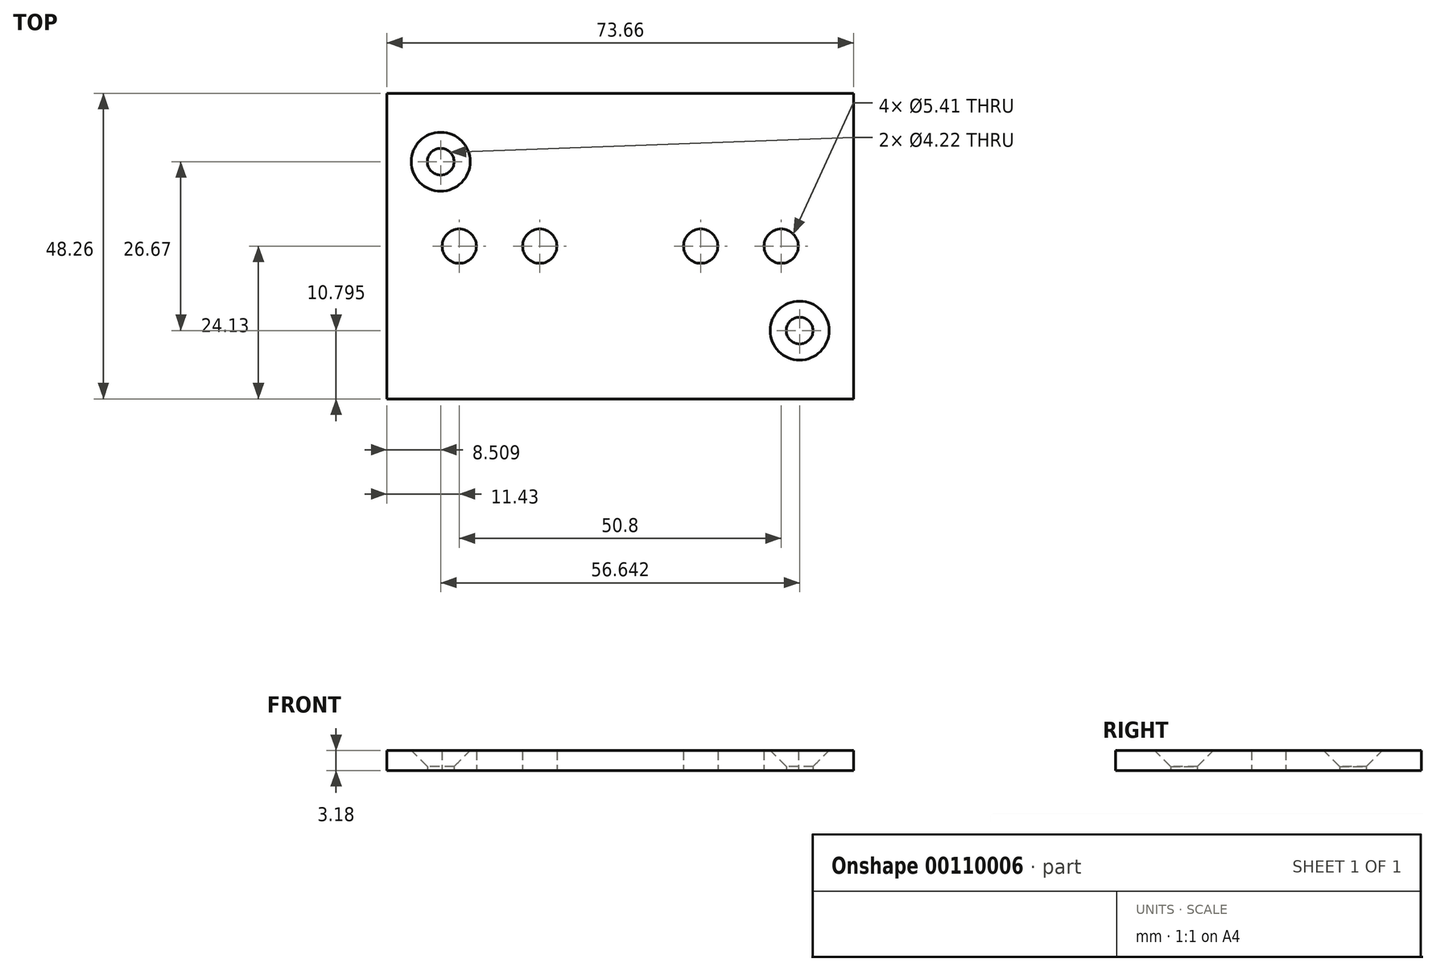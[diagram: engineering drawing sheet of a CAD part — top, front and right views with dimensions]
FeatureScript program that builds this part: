
annotation { "Feature Type Name" : "Feature", "Feature Type Description" : "" }
export const myFeature = defineFeature(function(context is Context, id is Id, definition is map)
    precondition{}
    {
        {
            var Q0;
            Q0=qCreatedBy(makeId("Top.planeOp"),FACE);
            var sketch = newSketch(context, id + "F0", { "sketchPlane" : qUnion([Q0])});
            skLineSegment(sketch, "E0.bottom", {"start": v(36.83, 24.13) * mm, "end": v(-36.83, 24.13) * mm});
            skLineSegment(sketch, "E0.top", {"start": v(36.83, -24.13) * mm, "end": v(-36.83, -24.13) * mm});
            skLineSegment(sketch, "E0.left", {"start": v(36.83, 24.13) * mm, "end": v(36.83, -24.13) * mm});
            skLineSegment(sketch, "E0.right", {"start": v(-36.83, 24.13) * mm, "end": v(-36.83, -24.13) * mm});
            skPoint(sketch, "E0.middle", {"position": v(0, 0) * mm});
            skCircle(sketch, "E1", {"center": v(28.32, -13.34) * mm, "radius": 2.1 * mm});
            skCircle(sketch, "E2", {"center": v(-28.32, 13.34) * mm, "radius": 2.1 * mm});
            skCircle(sketch, "E3", {"center": v(-25.4, 0) * mm, "radius": 2.7 * mm});
            skCircle(sketch, "E4", {"center": v(25.4, 0) * mm, "radius": 2.7 * mm});
            skCircle(sketch, "E5", {"center": v(12.7, 0) * mm, "radius": 2.7 * mm});
            skCircle(sketch, "E6", {"center": v(-12.7, 0) * mm, "radius": 2.7 * mm});
            skSolve(sketch);
        }
        {
            var Q0;
            Q0=makeQuery(id+"F0.imprint","IMPRINT",FACE,{"disambiguationData":[TD([[makeQuery(id+"F0.imprint","IMPRINT",EDGE,{"derivedFrom":sQuery(id+"F0.wireOp",EDGE,"E0.bottom")}),1.0]])]});
            extrude(context, id + "F1", {"entities" : qUnion([Q0]), "depth" : 3.17 * mm});
        }
        {
            var Q0;
            Q0=makeQuery(id+"F1.opExtrude","CAP_EDGE",EDGE,{"disambiguationData":[OSD([sQuery(id+"F0.wireOp",EDGE,"E2")])],"isStart":false});
            var Q1;
            Q1=makeQuery(id+"F1.opExtrude","CAP_EDGE",EDGE,{"disambiguationData":[OSD([sQuery(id+"F0.wireOp",EDGE,"E1")])],"isStart":false});
            chamfer(context, id + "F2", {"entities" : qUnion([Q0, Q1]), "width" : 2.54 * mm, "tangentPropagation" : true});
        }
    });
